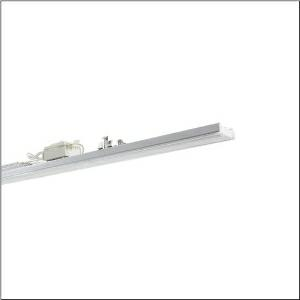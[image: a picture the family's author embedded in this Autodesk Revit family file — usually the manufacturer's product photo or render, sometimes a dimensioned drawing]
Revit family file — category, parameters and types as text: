
# Revit family: licross_r__21_recessed_mo_52tl1ede445gd_29f1
name_source: partatom
category: Lighting Fixtures
units: mm (PartAtom-declared; Revit-internal decimal feet)

## family parameters
Cut with Voids When Loaded = No
Host = Face
Light Source = No
Part Type = Normal
Room Calculation Point = No
Round Connector Dimension = Use Diameter
Shared = No

## types (1)
- --- (1 x LED, 750 lm, 5.3 W, 4000K)
    Apparent Load = 5 VA
    CIE Flux Codes = 85 95 99 100 100
    Color Rendering = 80
    Color Temperature = 4000K
    Default Elevation = 1800 mm
    Description = Licross® 21 Recessed MO, luminaire insert, of sheet steel, galvanised, coil coated, white, length: 750mm, width: 66mm, height: 67mm, LED rated luminous flux: 4.970lm, light colour: 840, control gear: DALI 2, with plug, 6-pole, with phase selection, mains connection: 220..240V, AC/DC, 0/50..60Hz, rated input power: 30W, without changeover relay, for emergency light function, for central battery installations according to DIN EN 60598-2-22, internal wiring halogen-free, primary light control with lens, of plastic, primary optical cover: cover, of PMMA, light emission: direct distribution, primary light characteristic: symmetric, protection rating (complete): IP40, insulation class (complete): insulation class I (protective earthing), certification: CE, ENEC, VDE, UKCA, protection symbol: D if used in an environment without relevant dust loads with corresponding accessories, impact resistance: IK06, permissible ambient temperature for indoor applications: -25..+35°C, standard: EN 60598-2-22, LABS conformity tested according to VDMA 24364:2018-05, reducing of maximum allowable ambient temperature of 5°C with ceiling mounting, corresponds to IFS (International Featured Standards) requirements for safety and quality in the food industry, packaging unit: 1 piece
    Height = 58 mm
    Lamp = 1 x LED
    Lamp Light Flux = 750 lm
    Lamp Power = 5.3 W
    Lamp count = 1
    Length = 750 mm  [stored 2.46063 ft]
    Luminous efficacy = 142 lm/W
    Manufacturer = Siteco
    ModVariant = No
    Model = 52TL1EDE445GD
    Mounting Place = Ceiling
    Mounting Type = Pendant
    Number of Poles = 1
    OnlyDefault = Yes
    Power Factor = 1
    Product Name = Licross® 21 Recessed MO
    Product group = luminaire insert | ceiling pendant
    ProductGroupID = 902
    Protection Class = Protection class I
    Protection Degree = IP 40
    RLX_Detail_Level = 1
    RLX_Emergency_Light_Flux = 0 lm
    RLX_Emergency_Type = 0
    RLX_Emergency_Type_DB = No
    RlxData = <blob elided: 29081 chars, md5=0c24745a>
    Socket = socket
    Standby Power = 0 W
    System Light Flux = 750 lm
    System Power = 5 W
    Type Comments = : DC mode (central or group accumulator) initial emergency light level
    Type Image = l_1296930.jpg
    URL = http://relux.com
    VarID = @adj_110887
    Voltage = 0 V
    Weight = 0.00 kg
    Width = 66 mm

note: [stored X ft] marks values corroborated as IEEE doubles in the binary element streams (Revit-internal decimal feet)

## geometry (parser evidence)
native form markers: Blend x4, Sweep x9
no freeform markers — native parametric forms only
